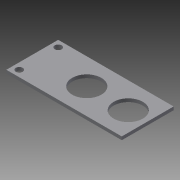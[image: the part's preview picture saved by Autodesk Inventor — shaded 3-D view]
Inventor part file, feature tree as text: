
AUTODESK INVENTOR PART (.ipt)
format: ipt  version: 2013 (Build 170138000, 138)  size: 89,600 bytes
history: native  units: in
note: dims shown in document units (in); Inventor stores cm internally (conversion verified against a paired STEP export)
features: extrude x1, sketch x1
ambient origin geometry x8: Origin, YZ Plane, XZ Plane, XY Plane, X Axis, Y Axis, Z Axis, Center Point
bodies: Solid1 (feature_tree)
feature tree (2):
  extrude  "Extrusion1"  Depth=0.266in
  sketch  "Sketch1"  dims[d0=1.125in d1=0.266in d2=0.266in d3=0.75in d4=0.75in d5=0.0in d6=3.45in d8=1.125in d9=1.6in d10=0.25in d11=0.25in d12=0.25in d13=0.75in d14=0.125in d15=0.0in]
